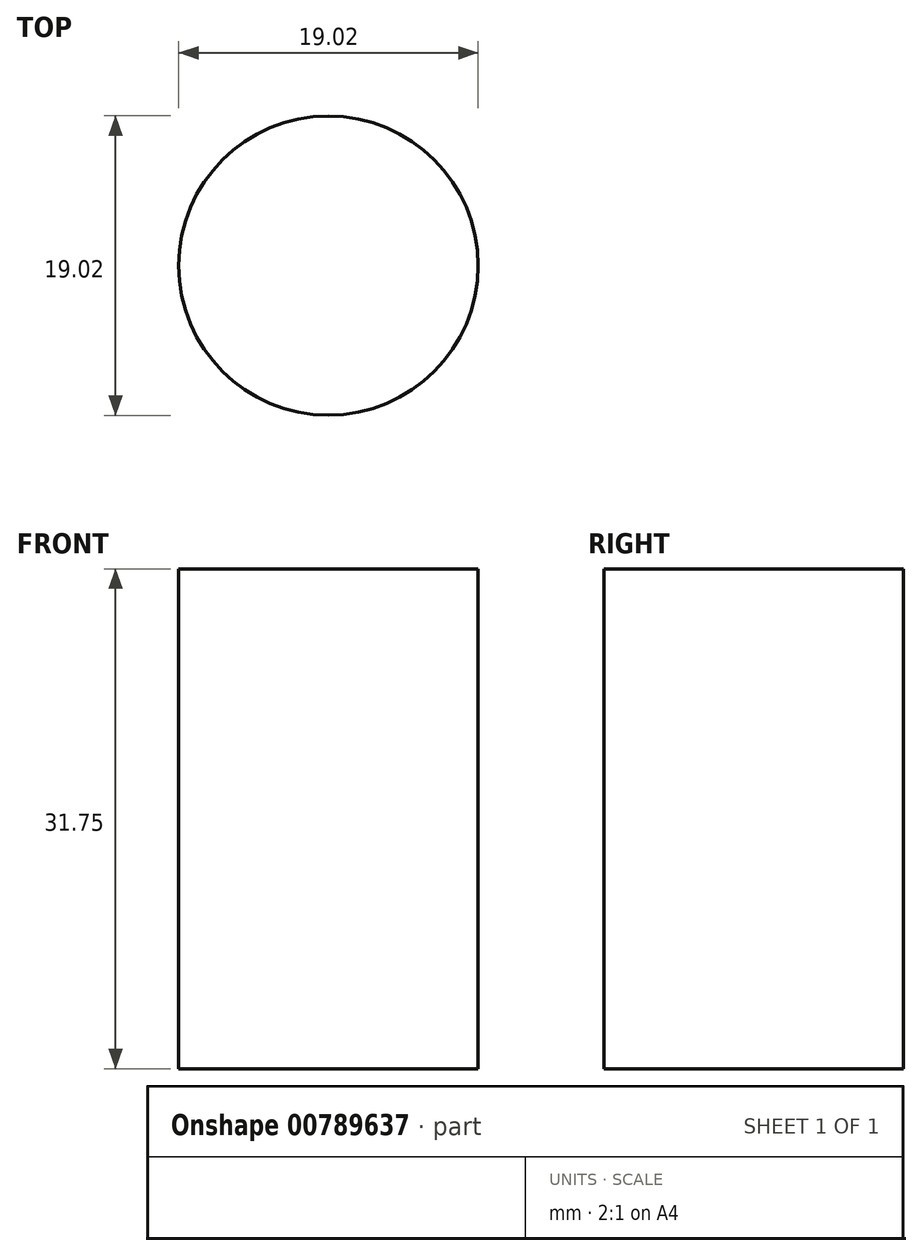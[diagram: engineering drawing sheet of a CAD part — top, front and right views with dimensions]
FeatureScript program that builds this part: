
annotation { "Feature Type Name" : "Feature", "Feature Type Description" : "" }
export const myFeature = defineFeature(function(context is Context, id is Id, definition is map)
    precondition{}
    {
        {
            var Q0;
            Q0=qCreatedBy(makeId("Top.planeOp"),FACE);
            var sketch = newSketch(context, id + "F0", { "sketchPlane" : qUnion([Q0])});
            skCircle(sketch, "E0", {"center": v(0, 0) * mm, "radius": 9.5 * mm});
            skSolve(sketch);
        }
        {
            var Q0;
            Q0=makeQuery(id+"F0.imprint","IMPRINT",FACE,{"disambiguationData":[TD([[makeQuery(id+"F0.imprint","IMPRINT",EDGE,{"derivedFrom":sQuery(id+"F0.wireOp",EDGE,"E0")}),1.0]])]});
            extrude(context, id + "F1", {"entities" : qUnion([Q0]), "depth" : 31.75 * mm, "offsetDistance" : 25.4 * mm});
        }
    });
